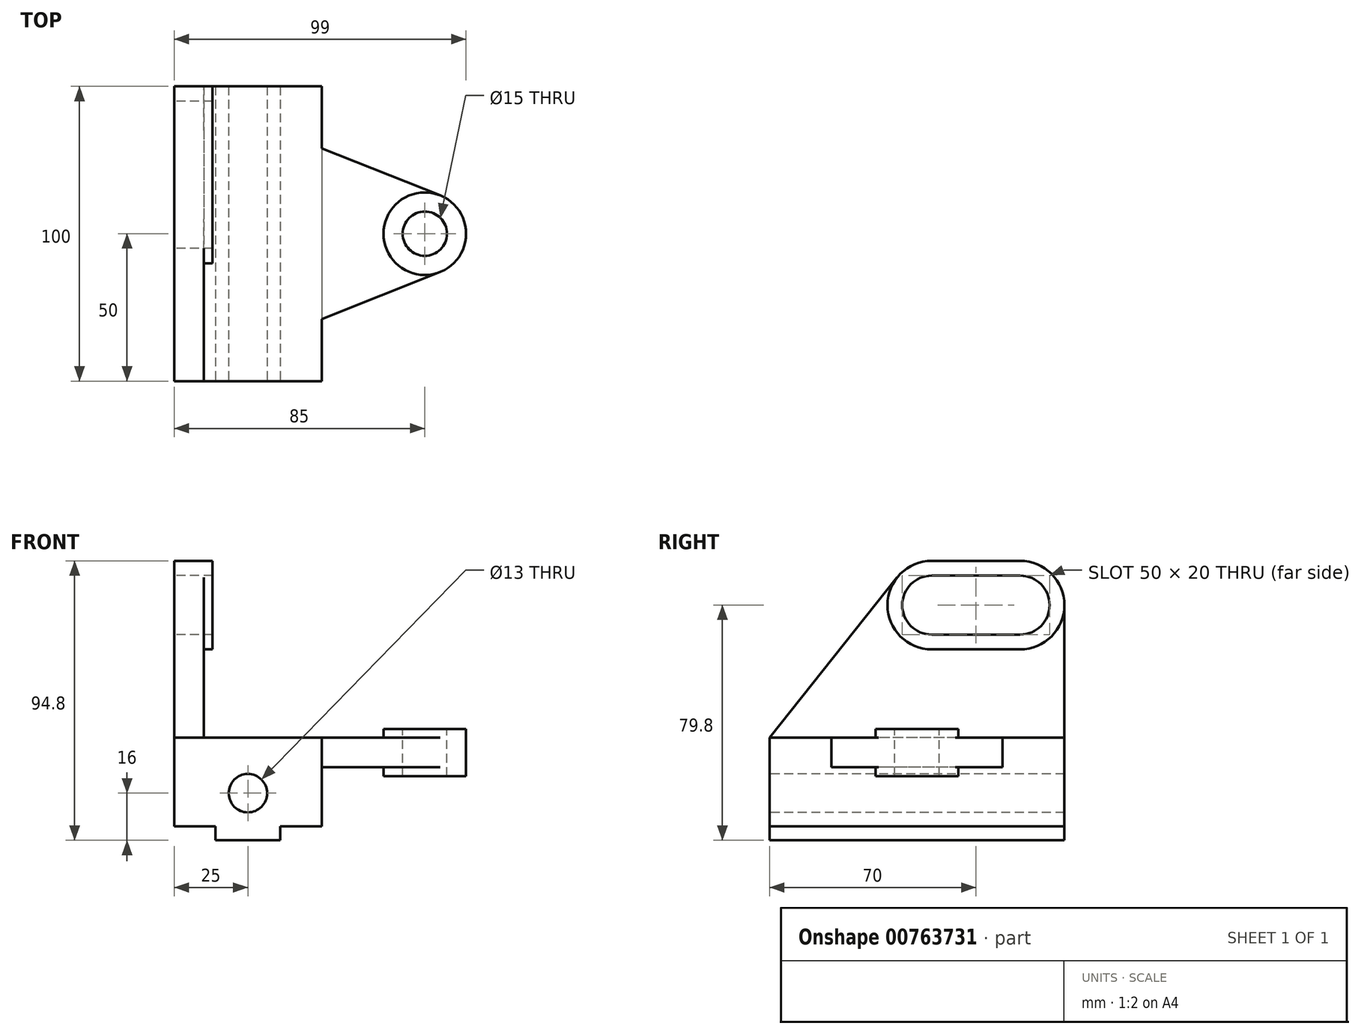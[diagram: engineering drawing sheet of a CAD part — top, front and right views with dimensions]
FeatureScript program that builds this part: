
annotation { "Feature Type Name" : "Feature", "Feature Type Description" : "" }
export const myFeature = defineFeature(function(context is Context, id is Id, definition is map)
    precondition{}
    {
        {
            var Q0;
            Q0=qCreatedBy(makeId("Front.planeOp"),FACE);
            var sketch = newSketch(context, id + "F0", { "sketchPlane" : qUnion([Q0])});
            skLineSegment(sketch, "E0", {"start": v(0, 0) * mm, "end": v(50, 0) * mm});
            skLineSegment(sketch, "E1", {"start": v(50, 0) * mm, "end": v(50, -30) * mm});
            skLineSegment(sketch, "E2", {"start": v(50, -30) * mm, "end": v(36, -30) * mm});
            skLineSegment(sketch, "E3", {"start": v(36, -30) * mm, "end": v(36, -34.8) * mm});
            skLineSegment(sketch, "E4", {"start": v(36, -34.8) * mm, "end": v(14, -34.8) * mm});
            skLineSegment(sketch, "E5", {"start": v(14, -34.8) * mm, "end": v(14, -30) * mm});
            skLineSegment(sketch, "E6", {"start": v(14, -30) * mm, "end": v(0, -30) * mm});
            skLineSegment(sketch, "E7", {"start": v(0, -30) * mm, "end": v(0, 0) * mm});
            skSolve(sketch);
        }
        {
            var Q0;
            Q0=makeQuery(id+"F0.imprint","IMPRINT",FACE,{"disambiguationData":[TD([[makeQuery(id+"F0.imprint","IMPRINT",EDGE,{"derivedFrom":sQuery(id+"F0.wireOp",EDGE,"E0")}),-1.0]])]});
            extrude(context, id + "F1", {"entities" : qUnion([Q0]), "depth" : 100 * mm, "offsetDistance" : 25 * mm});
        }
        {
            var Q0;
            Q0=makeQuery(id+"F1.opExtrude","SWEPT_FACE",FACE,{"disambiguationData":[OSD([sQuery(id+"F0.wireOp",EDGE,"E7")])]});
            var sketch = newSketch(context, id + "F2", { "sketchPlane" : qUnion([Q0])});
            skLineSegment(sketch, "E8", {"start": v(0, 0) * mm, "end": v(100, 0) * mm});
            skLineSegment(sketch, "E9", {"start": v(100, 0) * mm, "end": v(100, 45) * mm});
            skArc(sketch, "E10", {"start": v(100, 45) * mm, "mid": v(95.6, 55.6) * mm, "end": v(85, 60) * mm});
            skArc(sketch, "E11", {"start": v(55, 60) * mm, "mid": v(48.49, 58.51) * mm, "end": v(43.26, 54.34) * mm});
            skLineSegment(sketch, "E12", {"start": v(55, 60) * mm, "end": v(85, 60) * mm});
            skLineSegment(sketch, "E13", {"start": v(43.26, 54.34) * mm, "end": v(0, 0) * mm});
            skSolve(sketch);
        }
        {
            var Q0;
            Q0=makeQuery(id+"F2.imprint","IMPRINT",FACE,{"disambiguationData":[TD([[makeQuery(id+"F2.imprint","IMPRINT",EDGE,{"derivedFrom":sQuery(id+"F2.wireOp",EDGE,"E8")}),-1.0]])]});
            extrude(context, id + "F3", {"entities" : qUnion([Q0]), "operationType" : NewBodyOperationType.ADD, "oppositeDirection" : true, "depth" : 10 * mm, "offsetDistance" : 25 * mm});
        }
        {
            var Q0;
            Q0=makeQuery(id+"F1.opExtrude","CAP_FACE",FACE,{"disambiguationData":[OSD([sQuery(id+"F0.wireOp",EDGE,"E0"),sQuery(id+"F0.wireOp",EDGE,"E1"),sQuery(id+"F0.wireOp",EDGE,"E2"),sQuery(id+"F0.wireOp",EDGE,"E3"),sQuery(id+"F0.wireOp",EDGE,"E4"),sQuery(id+"F0.wireOp",EDGE,"E5"),sQuery(id+"F0.wireOp",EDGE,"E6"),sQuery(id+"F0.wireOp",EDGE,"E7")])],"isStart":true});
            var Q1;
            Q1=makeQuery(id+"F3.boolean.opBoolean","MERGE",FACE,{"derivedFrom":[makeQuery(id+"F1.opExtrude","CAP_FACE",FACE,{"disambiguationData":[OSD([sQuery(id+"F0.wireOp",EDGE,"E0"),sQuery(id+"F0.wireOp",EDGE,"E1"),sQuery(id+"F0.wireOp",EDGE,"E2"),sQuery(id+"F0.wireOp",EDGE,"E3"),sQuery(id+"F0.wireOp",EDGE,"E4"),sQuery(id+"F0.wireOp",EDGE,"E5"),sQuery(id+"F0.wireOp",EDGE,"E6"),sQuery(id+"F0.wireOp",EDGE,"E7")])],"isStart":false}),makeQuery(id+"F3.opExtrude","SWEPT_FACE",FACE,{"disambiguationData":[OSD([sQuery(id+"F2.wireOp",EDGE,"E9")])]})]});
            cPlane(context, id + "F4", {"entities" : qUnion([Q0, Q1]), "cplaneType" : CPlaneType.MID_PLANE, "offset" : 25 * mm, "width" : 150 * mm, "height" : 150 * mm});
        }
        {
            var Q0;
            Q0=makeQuery(id+"F1.opExtrude","SWEPT_BODY",BODY,{"disambiguationData":[OSD([sQuery(id+"F0.wireOp",EDGE,"E0"),sQuery(id+"F0.wireOp",EDGE,"E1"),sQuery(id+"F0.wireOp",EDGE,"E2"),sQuery(id+"F0.wireOp",EDGE,"E3"),sQuery(id+"F0.wireOp",EDGE,"E4"),sQuery(id+"F0.wireOp",EDGE,"E5"),sQuery(id+"F0.wireOp",EDGE,"E6"),sQuery(id+"F0.wireOp",EDGE,"E7")])]});
            var Q1;
            Q1=qCreatedBy(id+"F4.planeOp",FACE);
            mirror(context, id + "F5", {"entities" : qUnion([Q0]), "mirrorPlane" : qUnion([Q1])});
        }
        {
            var Q0;
            Q0=makeQuery(id+"F1.opExtrude","SWEPT_BODY",BODY,{"disambiguationData":[OSD([sQuery(id+"F0.wireOp",EDGE,"E0"),sQuery(id+"F0.wireOp",EDGE,"E1"),sQuery(id+"F0.wireOp",EDGE,"E2"),sQuery(id+"F0.wireOp",EDGE,"E3"),sQuery(id+"F0.wireOp",EDGE,"E4"),sQuery(id+"F0.wireOp",EDGE,"E5"),sQuery(id+"F0.wireOp",EDGE,"E6"),sQuery(id+"F0.wireOp",EDGE,"E7")])]});
            deleteBodies(context, id + "F6", {"entities" : qUnion([Q0])});
        }
        {
            var Q0;
            Q0=makeQuery(id+"F5.opPattern","COPY",FACE,{"derivedFrom":makeQuery(id+"F3.opExtrude","CAP_FACE",FACE,{"disambiguationData":[OSD([sQuery(id+"F2.wireOp",EDGE,"E8"),sQuery(id+"F2.wireOp",EDGE,"E9"),sQuery(id+"F2.wireOp",EDGE,"E10"),sQuery(id+"F2.wireOp",EDGE,"E11"),sQuery(id+"F2.wireOp",EDGE,"E12"),sQuery(id+"F2.wireOp",EDGE,"E13")])],"isStart":false}),"instanceName":"1"});
            var sketch = newSketch(context, id + "F7", { "sketchPlane" : qUnion([Q0])});
            skLineSegment(sketch, "E14", {"start": v(0, 0) * mm, "end": v(0, 45) * mm});
            skArc(sketch, "E15", {"start": v(-45, 60) * mm, "mid": v(-60, 45) * mm, "end": v(-45, 30) * mm});
            skArc(sketch, "E16", {"start": v(-15, 30) * mm, "mid": v(0, 45) * mm, "end": v(-15, 60) * mm});
            skLineSegment(sketch, "E17", {"start": v(-45, 60) * mm, "end": v(-15, 60) * mm});
            skLineSegment(sketch, "E18", {"start": v(-15, 30) * mm, "end": v(-45, 30) * mm});
            skArc(sketch, "E19", {"start": v(-45, 55) * mm, "mid": v(-55, 45) * mm, "end": v(-45, 35) * mm});
            skArc(sketch, "E20", {"start": v(-15, 35) * mm, "mid": v(-5, 45) * mm, "end": v(-15, 55) * mm});
            skLineSegment(sketch, "E21", {"start": v(-45, 45) * mm, "end": v(-45, 55) * mm});
            skLineSegment(sketch, "E22", {"start": v(-45, 55) * mm, "end": v(-15, 55) * mm});
            skLineSegment(sketch, "E23", {"start": v(-15, 55) * mm, "end": v(-15, 45) * mm});
            skLineSegment(sketch, "E24", {"start": v(-15, 45) * mm, "end": v(-15, 35) * mm});
            skLineSegment(sketch, "E25", {"start": v(-15, 35) * mm, "end": v(-45, 35) * mm});
            skSolve(sketch);
        }
        {
            var Q0;
            {var subQ3=sQuery(id+"F7.wireOp",EDGE,"E17");Q0=makeQuery(id+"F7.imprint","IMPRINT",FACE,{"disambiguationData":[TD([[makeQuery(id+"F7.imprint","IMPRINT",EDGE,{"derivedFrom":subQ3}),-1.0]])]});}
            extrude(context, id + "F8", {"entities" : qUnion([Q0]), "operationType" : NewBodyOperationType.ADD, "depth" : 3 * mm, "offsetDistance" : 25 * mm});
        }
        {
            var Q0;
            Q0=makeQuery(id+"F8.boolean.opBoolean","SPLIT",FACE,{"disambiguationData":[TD([makeQuery(id+"F8.opExtrude","SWEPT_FACE",FACE,{"disambiguationData":[OSD([sQuery(id+"F7.wireOp",EDGE,"E19")])]})])],"derivedFrom":makeQuery(id+"F5.opPattern","COPY",FACE,{"derivedFrom":makeQuery(id+"F3.opExtrude","CAP_FACE",FACE,{"disambiguationData":[OSD([sQuery(id+"F2.wireOp",EDGE,"E8"),sQuery(id+"F2.wireOp",EDGE,"E9"),sQuery(id+"F2.wireOp",EDGE,"E10"),sQuery(id+"F2.wireOp",EDGE,"E11"),sQuery(id+"F2.wireOp",EDGE,"E12"),sQuery(id+"F2.wireOp",EDGE,"E13")])],"isStart":false}),"instanceName":"1"})});
            var sketch = newSketch(context, id + "F9", { "sketchPlane" : qUnion([Q0])});
            skArc(sketch, "E26", {"start": v(-45, 55) * mm, "mid": v(-55, 45) * mm, "end": v(-45, 35) * mm});
            skArc(sketch, "E27", {"start": v(-15, 35) * mm, "mid": v(-5, 45) * mm, "end": v(-15, 55) * mm});
            skLineSegment(sketch, "E28", {"start": v(-15, 55) * mm, "end": v(-45, 55) * mm});
            skLineSegment(sketch, "E29", {"start": v(-45, 35) * mm, "end": v(-15, 35) * mm});
            skSolve(sketch);
        }
        {
            var Q0;
            Q0=makeQuery(id+"F9.imprint","IMPRINT",FACE,{"disambiguationData":[TD([[makeQuery(id+"F9.imprint","IMPRINT",EDGE,{"derivedFrom":sQuery(id+"F9.wireOp",EDGE,"E26")}),1.0]])]});
            extrude(context, id + "F10", {"entities" : qUnion([Q0]), "operationType" : NewBodyOperationType.REMOVE, "oppositeDirection" : true, "depth" : 25 * mm, "offsetDistance" : 25 * mm});
        }
        {
            var Q0;
            Q0=makeQuery(id+"F5.opPattern","COPY",FACE,{"derivedFrom":makeQuery(id+"F1.opExtrude","SWEPT_FACE",FACE,{"disambiguationData":[OSD([sQuery(id+"F0.wireOp",EDGE,"E0")])]}),"instanceName":"1"});
            var sketch = newSketch(context, id + "F11", { "sketchPlane" : qUnion([Q0])});
            skLineSegment(sketch, "E30", {"start": v(50, -100) * mm, "end": v(50, -50) * mm});
            skArc(sketch, "E31", {"start": v(90.18, -63) * mm, "mid": v(99, -50) * mm, "end": v(90.18, -37) * mm});
            skLineSegment(sketch, "E32", {"start": v(50, -50) * mm, "end": v(50, -21) * mm});
            skLineSegment(sketch, "E33", {"start": v(50, -21) * mm, "end": v(90.18, -37) * mm});
            skLineSegment(sketch, "E34.MirrorCS", {"start": v(50, -79) * mm, "end": v(90.18, -63) * mm});
            skSolve(sketch);
        }
        {
            var Q0;
            Q0=makeQuery(id+"F11.imprint","IMPRINT",FACE,{"disambiguationData":[TD([[makeQuery(id+"F11.imprint","IMPRINT",EDGE,{"derivedFrom":sQuery(id+"F11.wireOp",EDGE,"E31")}),1.0]])]});
            extrude(context, id + "F12", {"entities" : qUnion([Q0]), "operationType" : NewBodyOperationType.ADD, "oppositeDirection" : true, "depth" : 10 * mm, "offsetDistance" : 25 * mm});
        }
        {
            var Q0;
            Q0=makeQuery(id+"F12.opExtrude","CAP_FACE",FACE,{"disambiguationData":[OSD([sQuery(id+"F11.wireOp",EDGE,"E30"),sQuery(id+"F11.wireOp",EDGE,"E31"),sQuery(id+"F11.wireOp",EDGE,"E32"),sQuery(id+"F11.wireOp",EDGE,"E33"),sQuery(id+"F11.wireOp",EDGE,"E34.MirrorCS")])],"isStart":false});
            var Q1;
            Q1=makeQuery(id+"F12.boolean.opBoolean","MERGE",FACE,{"derivedFrom":[makeQuery(id+"F5.opPattern","COPY",FACE,{"derivedFrom":makeQuery(id+"F1.opExtrude","SWEPT_FACE",FACE,{"disambiguationData":[OSD([sQuery(id+"F0.wireOp",EDGE,"E0")])]}),"instanceName":"1"}),makeQuery(id+"F12.opExtrude","CAP_FACE",FACE,{"disambiguationData":[OSD([sQuery(id+"F11.wireOp",EDGE,"E30"),sQuery(id+"F11.wireOp",EDGE,"E31"),sQuery(id+"F11.wireOp",EDGE,"E32"),sQuery(id+"F11.wireOp",EDGE,"E33"),sQuery(id+"F11.wireOp",EDGE,"E34.MirrorCS")])],"isStart":true})]});
            cPlane(context, id + "F13", {"entities" : qUnion([Q0, Q1]), "cplaneType" : CPlaneType.MID_PLANE, "offset" : 25 * mm, "width" : 150 * mm, "height" : 150 * mm});
        }
        {
            var Q0;
            Q0=qCreatedBy(id+"F13.planeOp",FACE);
            var sketch = newSketch(context, id + "F14", { "sketchPlane" : qUnion([Q0])});
            skCircle(sketch, "E35", {"center": v(85, 50) * mm, "radius": 14 * mm});
            skCircle(sketch, "E36", {"center": v(85, 50) * mm, "radius": 7.5 * mm});
            skSolve(sketch);
        }
        {
            var Q0;
            Q0 = qSketchRegion(id + "F14", true);
            extrude(context, id + "F15", {"entities" : qUnion([Q0]), "operationType" : NewBodyOperationType.ADD, "endBound" : BoundingType.SYMMETRIC, "depth" : 16 * mm, "offsetDistance" : 25 * mm});
        }
        {
            var Q0;
            Q0=makeQuery(id+"F15.boolean.opBoolean","SPLIT",FACE,{"disambiguationData":[TD([makeQuery(id+"F15.opExtrude","SWEPT_FACE",FACE,{"disambiguationData":[OSD([sQuery(id+"F14.wireOp",EDGE,"E36")])]})])],"derivedFrom":makeQuery(id+"F12.boolean.opBoolean","MERGE",FACE,{"derivedFrom":[makeQuery(id+"F5.opPattern","COPY",FACE,{"derivedFrom":makeQuery(id+"F1.opExtrude","SWEPT_FACE",FACE,{"disambiguationData":[OSD([sQuery(id+"F0.wireOp",EDGE,"E0")])]}),"instanceName":"1"}),makeQuery(id+"F12.opExtrude","CAP_FACE",FACE,{"disambiguationData":[OSD([sQuery(id+"F11.wireOp",EDGE,"E30"),sQuery(id+"F11.wireOp",EDGE,"E31"),sQuery(id+"F11.wireOp",EDGE,"E32"),sQuery(id+"F11.wireOp",EDGE,"E33"),sQuery(id+"F11.wireOp",EDGE,"E34.MirrorCS")])],"isStart":true})]})});
            var sketch = newSketch(context, id + "F16", { "sketchPlane" : qUnion([Q0])});
            skCircle(sketch, "E37", {"center": v(85, -50) * mm, "radius": 7.5 * mm});
            skSolve(sketch);
        }
        {
            var Q0;
            Q0=makeQuery(id+"F16.imprint","IMPRINT",FACE,{"disambiguationData":[TD([[makeQuery(id+"F16.imprint","IMPRINT",EDGE,{"derivedFrom":sQuery(id+"F16.wireOp",EDGE,"E37")}),-1.0]])]});
            extrude(context, id + "F17", {"entities" : qUnion([Q0]), "operationType" : NewBodyOperationType.REMOVE, "oppositeDirection" : true, "depth" : 25 * mm, "offsetDistance" : 25 * mm});
        }
        {
            var Q0;
            Q0=makeQuery(id+"F5.opPattern","COPY",FACE,{"derivedFrom":makeQuery(id+"F1.opExtrude","CAP_FACE",FACE,{"disambiguationData":[OSD([sQuery(id+"F0.wireOp",EDGE,"E0"),sQuery(id+"F0.wireOp",EDGE,"E1"),sQuery(id+"F0.wireOp",EDGE,"E2"),sQuery(id+"F0.wireOp",EDGE,"E3"),sQuery(id+"F0.wireOp",EDGE,"E4"),sQuery(id+"F0.wireOp",EDGE,"E5"),sQuery(id+"F0.wireOp",EDGE,"E6"),sQuery(id+"F0.wireOp",EDGE,"E7")])],"isStart":true}),"instanceName":"1"});
            var sketch = newSketch(context, id + "F18", { "sketchPlane" : qUnion([Q0])});
            skLineSegment(sketch, "E38", {"start": v(0, -30) * mm, "end": v(25, -30) * mm});
            skLineSegment(sketch, "E39", {"start": v(25, -30) * mm, "end": v(25, -34.8) * mm});
            skLineSegment(sketch, "E40", {"start": v(25, -34.8) * mm, "end": v(25, -18.8) * mm});
            skPoint(sketch, "E41", {"position": v(25, -18.8) * mm});
            skSolve(sketch);
        }
        {
            var Q0;
            Q0=sQuery(id+"F18.wireOp",VERTEX,"E41");
            var Q1;
            Q1=makeQuery(id+"F5.opPattern","COPY",BODY,{"derivedFrom":makeQuery(id+"F1.opExtrude","SWEPT_BODY",BODY,{"disambiguationData":[OSD([sQuery(id+"F0.wireOp",EDGE,"E0"),sQuery(id+"F0.wireOp",EDGE,"E1"),sQuery(id+"F0.wireOp",EDGE,"E2"),sQuery(id+"F0.wireOp",EDGE,"E3"),sQuery(id+"F0.wireOp",EDGE,"E4"),sQuery(id+"F0.wireOp",EDGE,"E5"),sQuery(id+"F0.wireOp",EDGE,"E6"),sQuery(id+"F0.wireOp",EDGE,"E7")])]}),"instanceName":"1"});
            hole(context, id + "F19", {"style" : HoleStyle.SIMPLE, "endStyle" : HoleEndStyle.THROUGH, "holeDiameter" : 13 * mm, "majorDiameter" : 5 * mm, "isTappedThrough" : true, "tappedDepth" : 12 * mm, "tapClearance" : 3, "locations" : qUnion([Q0]), "scope" : qUnion([Q1])});
        }
    });
